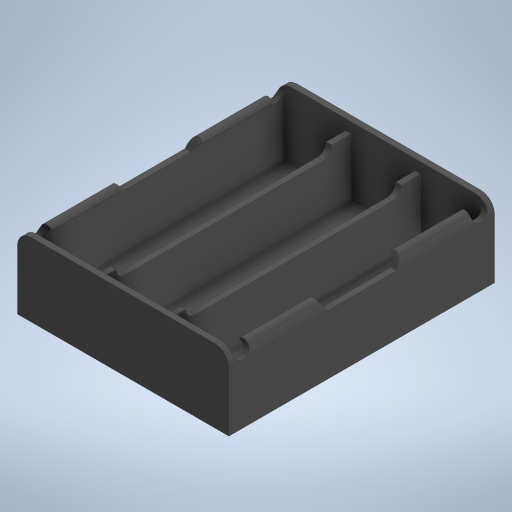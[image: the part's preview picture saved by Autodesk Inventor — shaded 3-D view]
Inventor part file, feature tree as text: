
AUTODESK INVENTOR PART (.ipt)
format: ipt  version: 2023.1 (Build 271208000, 208)  size: 377,344 bytes
history: native  units: mm
features: extrude x5, sketch x4, other x2, mirror x2, fillet x1
ambient origin geometry x8: Origin, YZ Plane, XZ Plane, XY Plane, X Axis, Y Axis, Z Axis, Center Point
bodies: Body1 (feature_tree), Body2 (feature_tree), Body3 (feature_tree)
feature tree (14):
  other  "솔리드1"
  sketch  "스케치1"
  extrude  "돌출1"  Depth=60.5mm
  extrude  "돌출2"  Depth=21.0mm
  extrude  "돌출3"  Depth=76.0mm TaperAngle=0.0deg
  mirror  "미러1"
  extrude  "돌출4"  Depth=4.0mm
  fillet  "모깎기1"  Radius=1.6mm
  other  "작업 평면1"
  extrude  "돌출5"  Depth=53.6mm
  mirror  "미러2"
  sketch  "스케치2"
  sketch  "스케치3"
  sketch  "스케치5"
